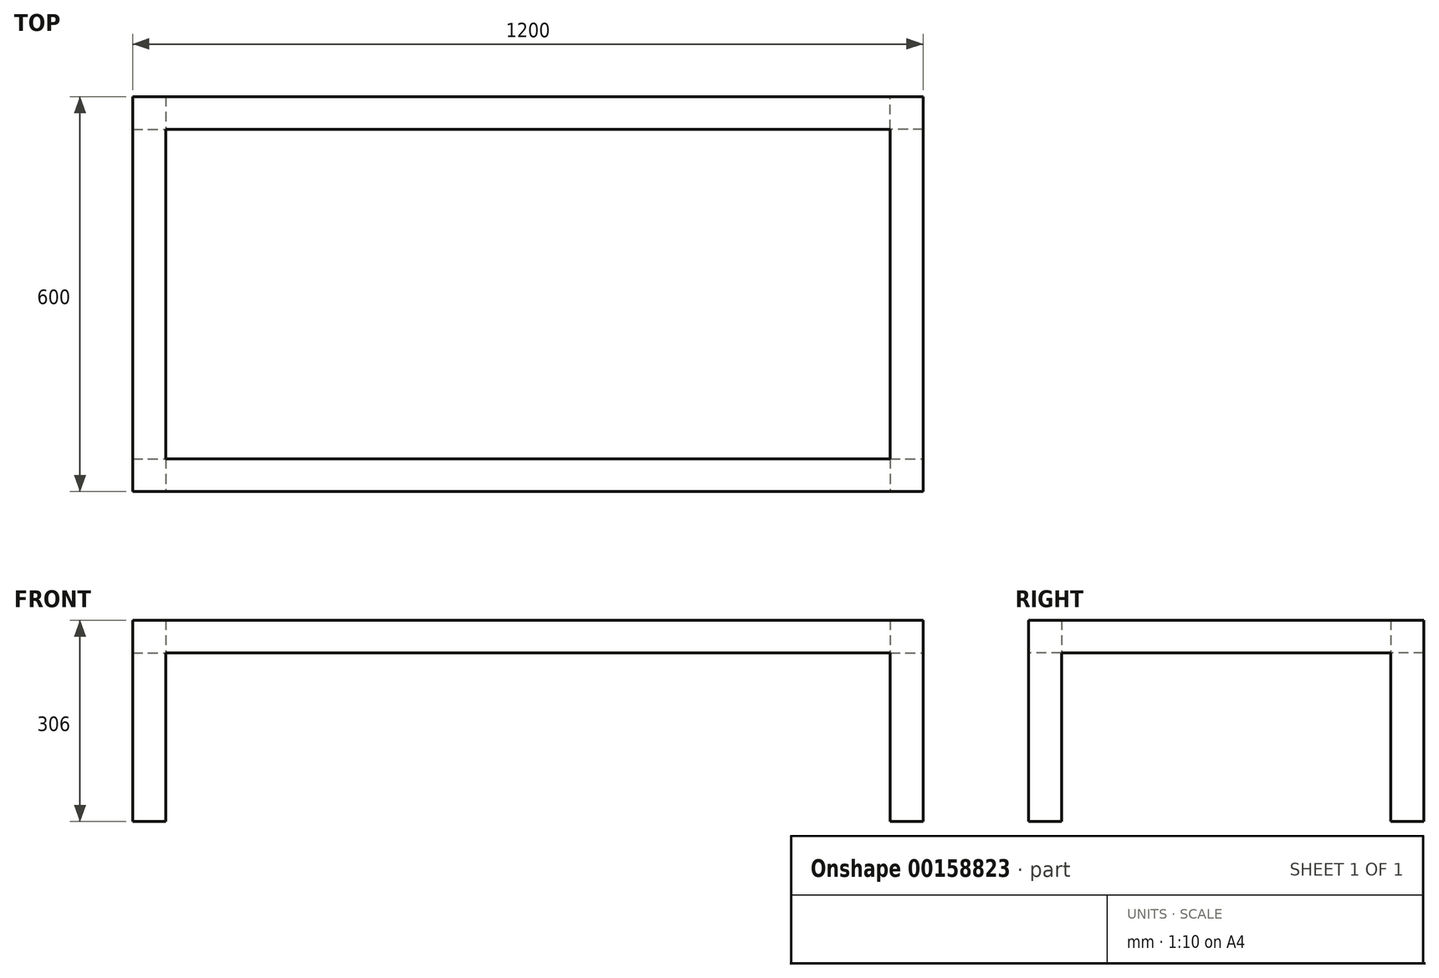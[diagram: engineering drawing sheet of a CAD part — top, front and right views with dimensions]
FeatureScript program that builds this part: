
annotation { "Feature Type Name" : "Feature", "Feature Type Description" : "" }
export const myFeature = defineFeature(function(context is Context, id is Id, definition is map)
    precondition{}
    {
        {
            var Q0;
            Q0=qCreatedBy(makeId("Top.planeOp"),FACE);
            var sketch = newSketch(context, id + "F0", { "sketchPlane" : qUnion([Q0])});
            skLineSegment(sketch, "E0.bottom", {"start": v(0, 0) * mm, "end": v(50, 0) * mm});
            skLineSegment(sketch, "E0.top", {"start": v(0, -50) * mm, "end": v(50, -50) * mm});
            skLineSegment(sketch, "E0.left", {"start": v(0, 0) * mm, "end": v(0, -50) * mm});
            skLineSegment(sketch, "E0.right", {"start": v(50, 0) * mm, "end": v(50, -50) * mm});
            skLineSegment(sketch, "E1.bottom", {"start": v(0, 550) * mm, "end": v(50, 550) * mm});
            skLineSegment(sketch, "E1.top", {"start": v(0, 500) * mm, "end": v(50, 500) * mm});
            skLineSegment(sketch, "E1.left", {"start": v(0, 550) * mm, "end": v(0, 500) * mm});
            skLineSegment(sketch, "E1.right", {"start": v(50, 550) * mm, "end": v(50, 500) * mm});
            skLineSegment(sketch, "E2.bottom", {"start": v(1150, 0) * mm, "end": v(1200, 0) * mm});
            skLineSegment(sketch, "E2.top", {"start": v(1150, -50) * mm, "end": v(1200, -50) * mm});
            skLineSegment(sketch, "E2.left", {"start": v(1150, 0) * mm, "end": v(1150, -50) * mm});
            skLineSegment(sketch, "E2.right", {"start": v(1200, 0) * mm, "end": v(1200, -50) * mm});
            skLineSegment(sketch, "E3.bottom", {"start": v(1200, 500) * mm, "end": v(1150, 500) * mm});
            skLineSegment(sketch, "E3.top", {"start": v(1200, 550) * mm, "end": v(1150, 550) * mm});
            skLineSegment(sketch, "E3.left", {"start": v(1200, 500) * mm, "end": v(1200, 550) * mm});
            skLineSegment(sketch, "E3.right", {"start": v(1150, 500) * mm, "end": v(1150, 550) * mm});
            skSolve(sketch);
        }
        {
            var Q0;
            Q0=qSketchRegion(id+"F0",true);
            extrude(context, id + "F1", {"entities" : qUnion([Q0]), "depth" : 256 * mm});
        }
        {
            var Q0;
            Q0=makeQuery(id+"F1.opExtrude","CAP_FACE",FACE,{"disambiguationData":[OSD([sQuery(id+"F0.wireOp",EDGE,"E0.bottom"),sQuery(id+"F0.wireOp",EDGE,"E0.top"),sQuery(id+"F0.wireOp",EDGE,"E0.left"),sQuery(id+"F0.wireOp",EDGE,"E0.right")])],"isStart":false});
            var sketch = newSketch(context, id + "F2", { "sketchPlane" : qUnion([Q0])});
            skLineSegment(sketch, "E4.bottom", {"start": v(50, 0) * mm, "end": v(1150, 0) * mm});
            skLineSegment(sketch, "E4.top", {"start": v(0, -50) * mm, "end": v(1200, -50) * mm});
            skLineSegment(sketch, "E4.left", {"start": v(0, 0) * mm, "end": v(0, -50) * mm});
            skLineSegment(sketch, "E4.right", {"start": v(1200, 0) * mm, "end": v(1200, -50) * mm});
            skLineSegment(sketch, "E5.bottom", {"start": v(1200, -50) * mm, "end": v(1150, -50) * mm});
            skLineSegment(sketch, "E5.top", {"start": v(1200, 550) * mm, "end": v(1150, 550) * mm});
            skLineSegment(sketch, "E5.left", {"start": v(1200, -50) * mm, "end": v(1200, 550) * mm});
            skLineSegment(sketch, "E5.right", {"start": v(1150, 0) * mm, "end": v(1150, 500) * mm});
            skLineSegment(sketch, "E6.bottom", {"start": v(1200, 550) * mm, "end": v(0, 550) * mm});
            skLineSegment(sketch, "E6.top", {"start": v(1150, 500) * mm, "end": v(50, 500) * mm});
            skLineSegment(sketch, "E6.left", {"start": v(1200, 550) * mm, "end": v(1200, 500) * mm});
            skLineSegment(sketch, "E6.right", {"start": v(0, 550) * mm, "end": v(0, 500) * mm});
            skLineSegment(sketch, "E7.bottom", {"start": v(0, 550) * mm, "end": v(50, 550) * mm});
            skLineSegment(sketch, "E7.top", {"start": v(0, -50) * mm, "end": v(50, -50) * mm});
            skLineSegment(sketch, "E7.left", {"start": v(0, 550) * mm, "end": v(0, -50) * mm});
            skLineSegment(sketch, "E7.right", {"start": v(50, 500) * mm, "end": v(50, 0) * mm});
            skSolve(sketch);
        }
        {
            var Q0;
            Q0=qSketchRegion(id+"F2",true);
            extrude(context, id + "F3", {"entities" : qUnion([Q0]), "operationType" : NewBodyOperationType.ADD, "depth" : 50 * mm});
        }
    });
